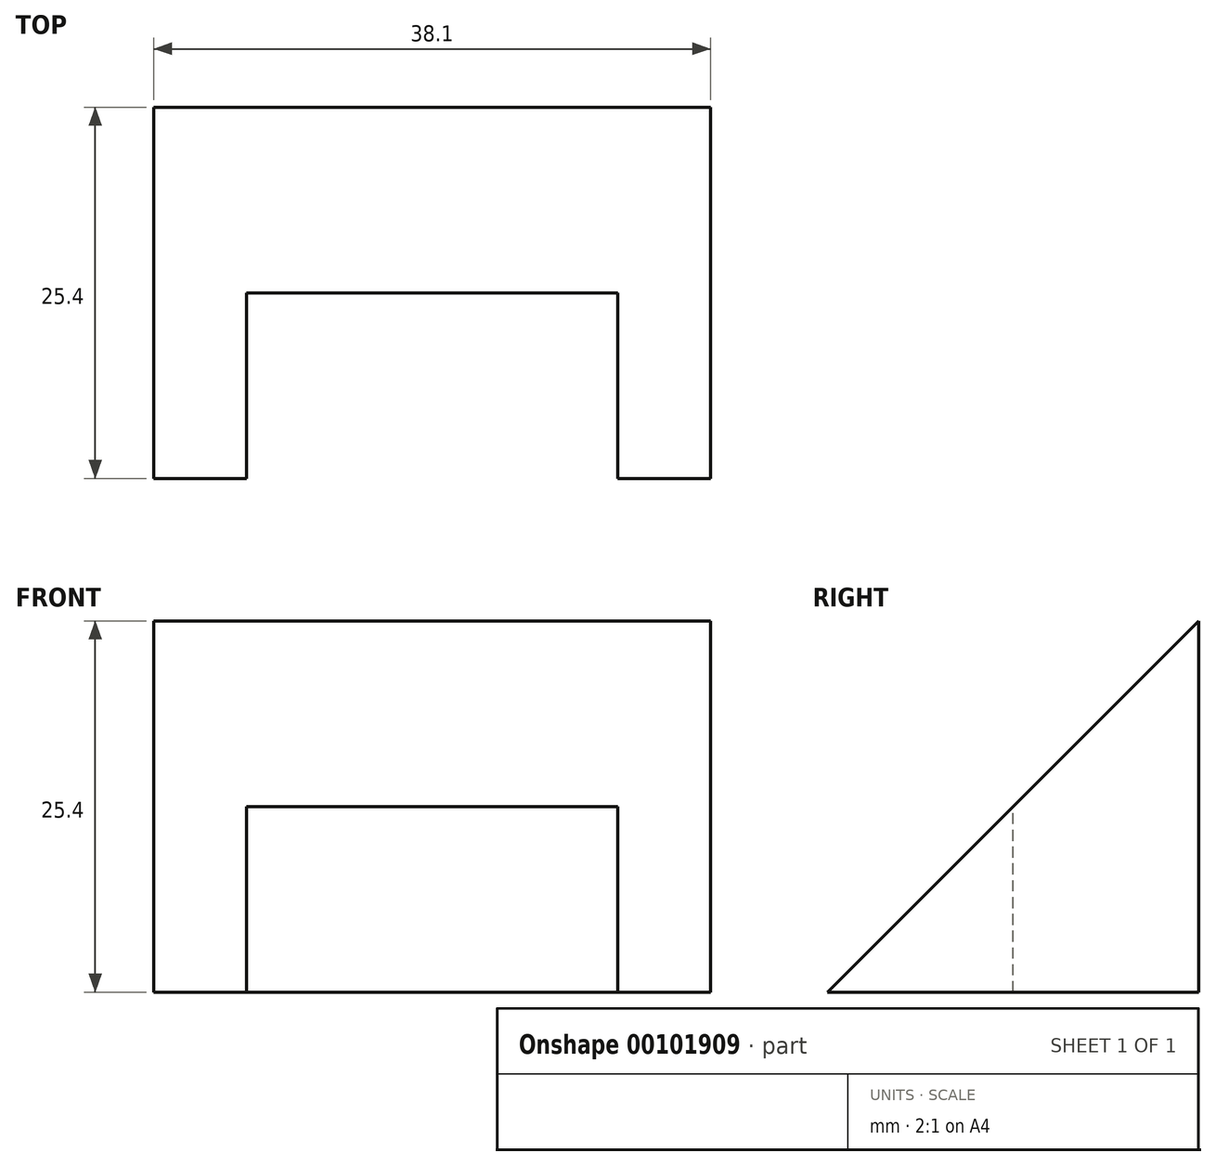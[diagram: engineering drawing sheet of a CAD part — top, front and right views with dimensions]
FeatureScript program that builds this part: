
annotation { "Feature Type Name" : "Feature", "Feature Type Description" : "" }
export const myFeature = defineFeature(function(context is Context, id is Id, definition is map)
    precondition{}
    {
        {
            var Q0;
            Q0=qCreatedBy(makeId("Right.planeOp"),FACE);
            var sketch = newSketch(context, id + "F0", { "sketchPlane" : qUnion([Q0])});
            skLineSegment(sketch, "E0", {"start": v(-12.7, -12.7) * mm, "end": v(12.7, 12.7) * mm});
            skLineSegment(sketch, "E1", {"start": v(12.7, 12.7) * mm, "end": v(12.7, -12.7) * mm});
            skLineSegment(sketch, "E2", {"start": v(12.7, -12.7) * mm, "end": v(-12.7, -12.7) * mm});
            skPoint(sketch, "E3", {"position": v(0, 0) * mm});
            skSolve(sketch);
        }
        {
            var Q0;
            Q0 = qSketchRegion(id + "F0", true);
            extrude(context, id + "F1", {"entities" : qUnion([Q0]), "depth" : 38.1 * mm});
        }
        {
            var Q0;
            Q0=qCreatedBy(makeId("Top.planeOp"),FACE);
            var sketch = newSketch(context, id + "F2", { "sketchPlane" : qUnion([Q0])});
            skLineSegment(sketch, "E4.bottom", {"start": v(6.35, 0) * mm, "end": v(31.75, 0) * mm});
            skLineSegment(sketch, "E4.top", {"start": v(6.35, -12.7) * mm, "end": v(31.75, -12.7) * mm});
            skLineSegment(sketch, "E4.left", {"start": v(6.35, 0) * mm, "end": v(6.35, -12.7) * mm});
            skLineSegment(sketch, "E4.right", {"start": v(31.75, 0) * mm, "end": v(31.75, -12.7) * mm});
            skSolve(sketch);
        }
        {
            var Q0;
            Q0 = qSketchRegion(id + "F2", true);
            extrude(context, id + "F3", {"entities" : qUnion([Q0]), "operationType" : NewBodyOperationType.REMOVE, "endBound" : BoundingType.THROUGH_ALL, "oppositeDirection" : true, "depth" : 25.4 * mm});
        }
    });
